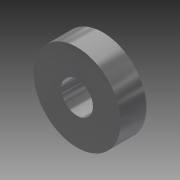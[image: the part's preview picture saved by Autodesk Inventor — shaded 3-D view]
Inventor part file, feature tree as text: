
AUTODESK INVENTOR PART (.ipt)
format: ipt  version: 2014 (Build 180170000, 170)  size: 80,384 bytes
history: native  units: in
note: dims shown in document units (in); Inventor stores cm internally (conversion verified against a paired STEP export)
features: extrude x1, sketch x1
ambient origin geometry x8: Origin, YZ Plane, XZ Plane, XY Plane, X Axis, Y Axis, Z Axis, Center Point
bodies: Solid1 (feature_tree)
feature tree (2):
  extrude  "Extrusion1"  Depth=0.55in
  sketch  "Sketch1"  dims[d0=1.85in d1=0.675in d2=0.55in d3=0.0in]
